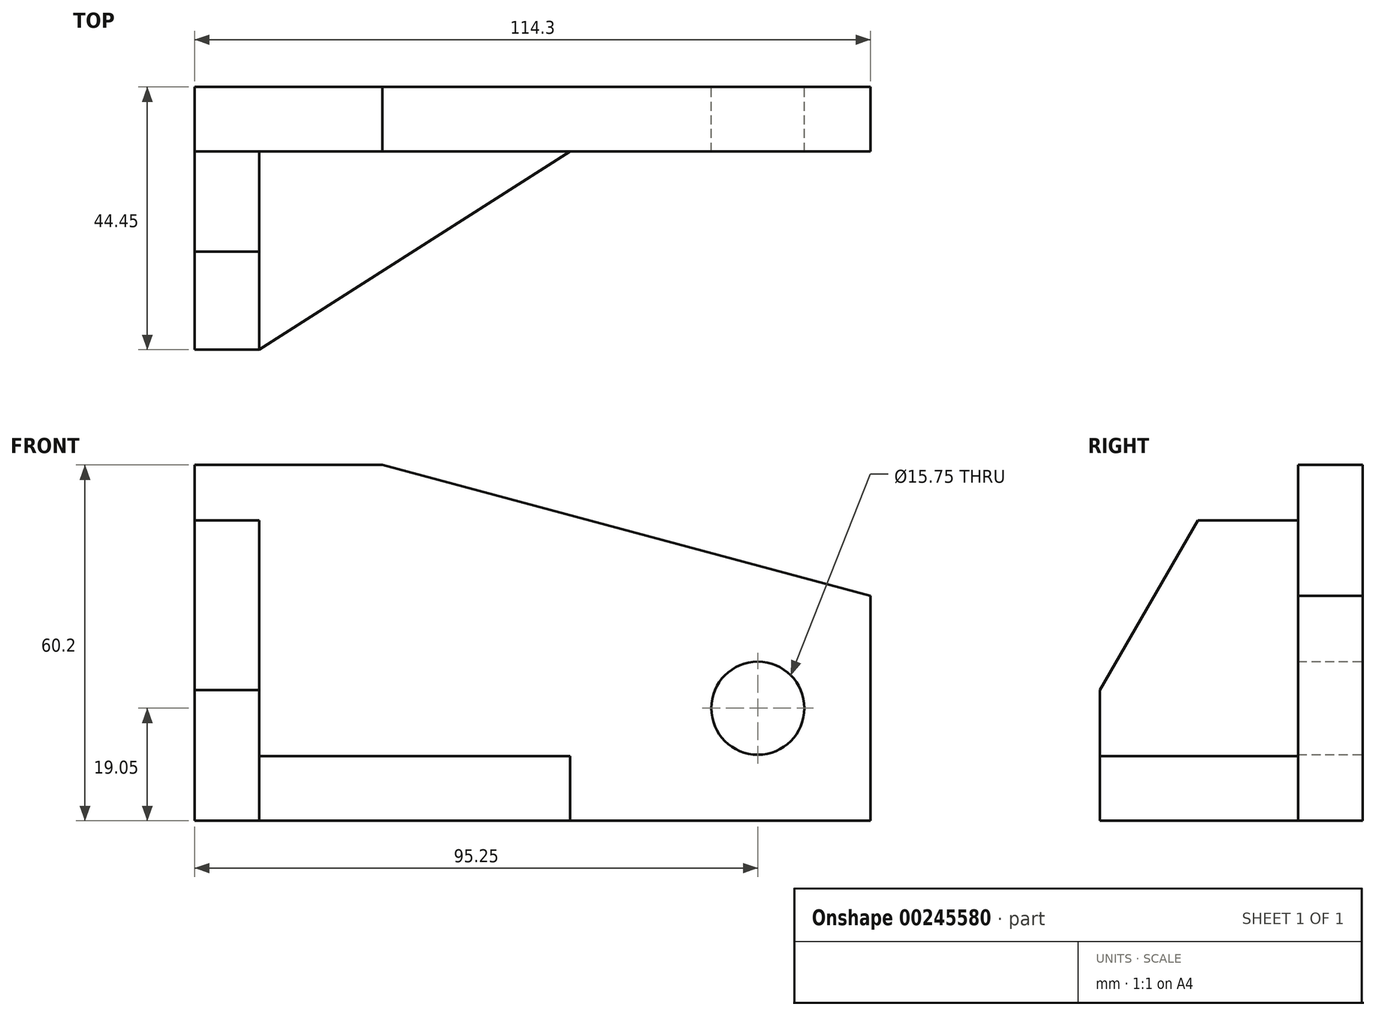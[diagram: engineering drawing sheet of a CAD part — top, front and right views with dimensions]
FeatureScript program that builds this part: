
annotation { "Feature Type Name" : "Feature", "Feature Type Description" : "" }
export const myFeature = defineFeature(function(context is Context, id is Id, definition is map)
    precondition{}
    {
        {
            var Q0;
            Q0=qCreatedBy(makeId("Front.planeOp"),FACE);
            var sketch = newSketch(context, id + "F0", { "sketchPlane" : qUnion([Q0])});
            skCircle(sketch, "E0", {"center": v(0, 0) * mm, "radius": 7.87 * mm});
            skLineSegment(sketch, "E1", {"start": v(-95.25, -19.05) * mm, "end": v(19.05, -19.05) * mm});
            skLineSegment(sketch, "E2", {"start": v(19.05, -19.05) * mm, "end": v(19.05, 19.03) * mm});
            skLineSegment(sketch, "E3", {"start": v(-95.25, -19.05) * mm, "end": v(-95.25, 41.15) * mm});
            skLineSegment(sketch, "E4", {"start": v(-95.25, 41.15) * mm, "end": v(-63.5, 41.15) * mm});
            skLineSegment(sketch, "E5", {"start": v(-63.5, 41.15) * mm, "end": v(19.05, 19.03) * mm});
            skSolve(sketch);
        }
        {
            var Q0;
            Q0=makeQuery(id+"F0.imprint","IMPRINT",FACE,{"disambiguationData":[TD([[makeQuery(id+"F0.imprint","IMPRINT",EDGE,{"derivedFrom":sQuery(id+"F0.wireOp",EDGE,"E0")}),-1.0]])]});
            extrude(context, id + "F1", {"entities" : qUnion([Q0]), "depth" : 10.92 * mm});
        }
        {
            var Q0;
            Q0=makeQuery(id+"F1.opExtrude","SWEPT_FACE",FACE,{"disambiguationData":[OSD([sQuery(id+"F0.wireOp",EDGE,"E3")])]});
            var sketch = newSketch(context, id + "F2", { "sketchPlane" : qUnion([Q0])});
            skLineSegment(sketch, "E6", {"start": v(10.92, -19.05) * mm, "end": v(10.92, 31.75) * mm});
            skLineSegment(sketch, "E7", {"start": v(0, -19.05) * mm, "end": v(44.45, -19.05) * mm});
            skPoint(sketch, "E7.endSnap0", {"position": v(5.46, -19.05) * mm});
            skLineSegment(sketch, "E8", {"start": v(44.45, -19.05) * mm, "end": v(44.45, 3.05) * mm});
            skLineSegment(sketch, "E9", {"start": v(10.92, 31.75) * mm, "end": v(27.88, 31.75) * mm});
            skLineSegment(sketch, "E10", {"start": v(27.88, 31.75) * mm, "end": v(44.45, 3.05) * mm});
            skSolve(sketch);
        }
        {
            var Q0;
            {var subQ2=sQuery(id+"F2.wireOp",EDGE,"E6");Q0=makeQuery(id+"F2.imprint","IMPRINT",FACE,{"disambiguationData":[TD([[makeQuery(id+"F2.imprint","IMPRINT",EDGE,{"derivedFrom":subQ2}),-1.0]])]});}
            extrude(context, id + "F3", {"entities" : qUnion([Q0]), "operationType" : NewBodyOperationType.ADD, "oppositeDirection" : true, "depth" : 10.92 * mm});
        }
        {
            var Q0;
            Q0=makeQuery(id+"F3.boolean.opBoolean","MERGE",FACE,{"derivedFrom":[makeQuery(id+"F1.opExtrude","SWEPT_FACE",FACE,{"disambiguationData":[OSD([sQuery(id+"F0.wireOp",EDGE,"E1")])]}),makeQuery(id+"F3.opExtrude","SWEPT_FACE",FACE,{"disambiguationData":[OSD([sQuery(id+"F2.wireOp",EDGE,"E7")])]})]});
            var sketch = newSketch(context, id + "F4", { "sketchPlane" : qUnion([Q0])});
            skLineSegment(sketch, "E11", {"start": v(-95.25, 10.92) * mm, "end": v(-31.75, 10.92) * mm});
            skLineSegment(sketch, "E12", {"start": v(-84.33, 44.45) * mm, "end": v(-31.75, 10.92) * mm});
            skSolve(sketch);
        }
        {
            var Q0;
            {var subQ2=sQuery(id+"F4.wireOp",EDGE,"E12");Q0=makeQuery(id+"F4.imprint","IMPRINT",FACE,{"disambiguationData":[TD([[makeQuery(id+"F4.imprint","IMPRINT",EDGE,{"derivedFrom":subQ2}),-1.0]])]});}
            extrude(context, id + "F5", {"entities" : qUnion([Q0]), "operationType" : NewBodyOperationType.ADD, "oppositeDirection" : true, "depth" : 10.92 * mm});
        }
    });
